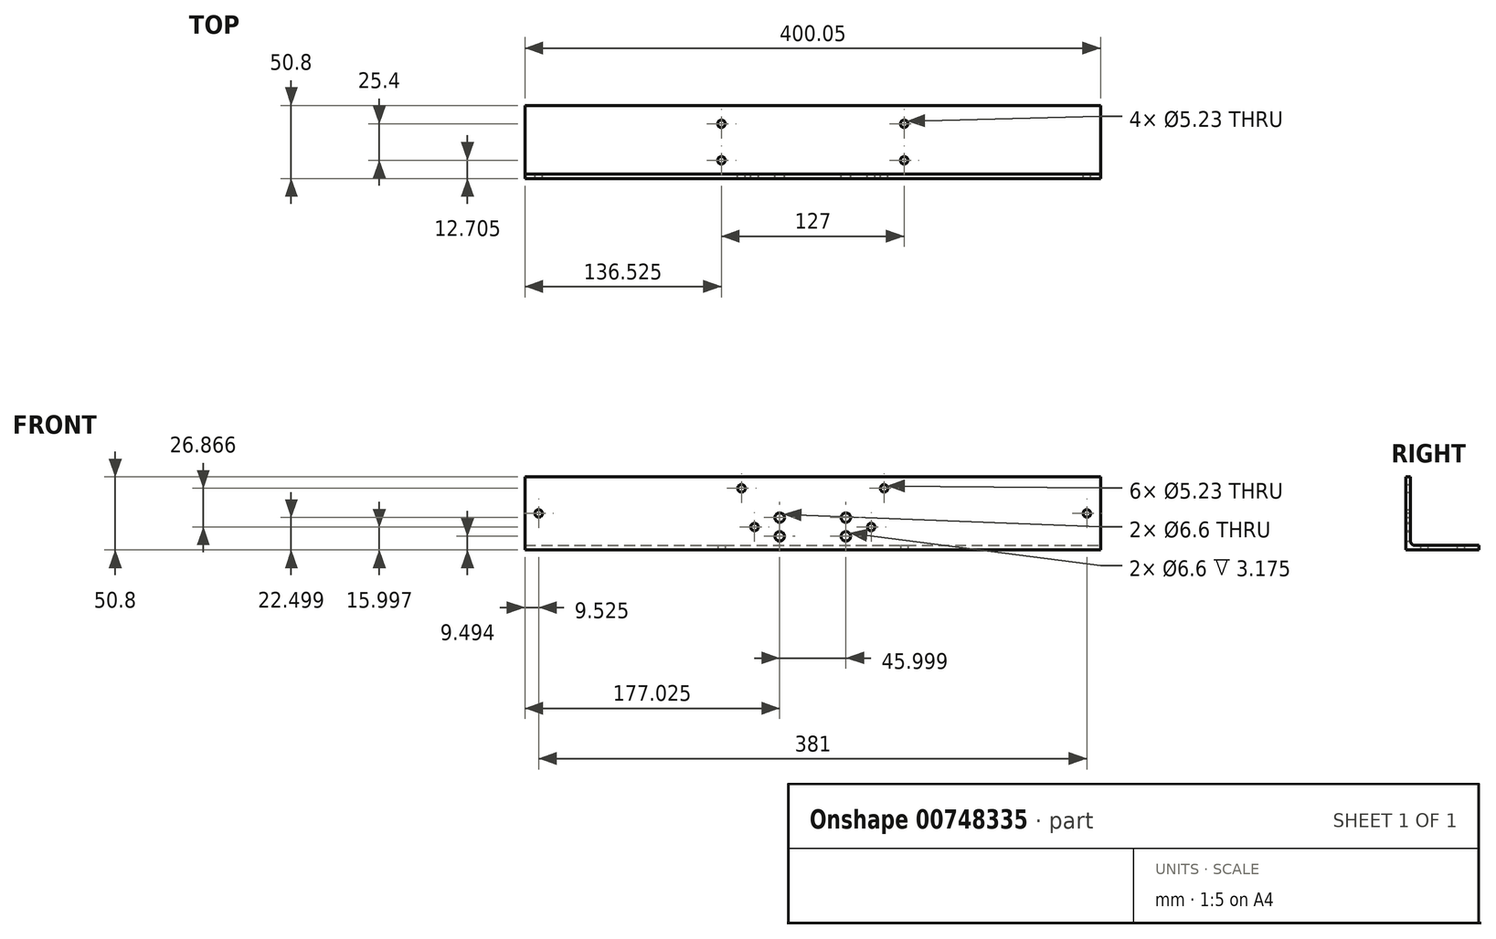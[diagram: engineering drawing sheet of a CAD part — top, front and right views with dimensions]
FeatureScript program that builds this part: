
annotation { "Feature Type Name" : "Feature", "Feature Type Description" : "" }
export const myFeature = defineFeature(function(context is Context, id is Id, definition is map)
    precondition{}
    {
        {
            var Q0;
            Q0=qCreatedBy(makeId("Right.planeOp"),FACE);
            var sketch = newSketch(context, id + "F0", { "sketchPlane" : qUnion([Q0])});
            skLineSegment(sketch, "E0", {"start": v(0, 0) * mm, "end": v(0, -44.45) * mm});
            skLineSegment(sketch, "E1", {"start": v(3.18, -47.63) * mm, "end": v(47.63, -47.62) * mm});
            skLineSegment(sketch, "E2.0", {"start": v(-3.17, -50.8) * mm, "end": v(47.63, -50.8) * mm});
            skLineSegment(sketch, "E2.1", {"start": v(-3.18, 0) * mm, "end": v(-3.17, -50.8) * mm});
            skLineSegment(sketch, "E3", {"start": v(-3.18, 0) * mm, "end": v(0, 0) * mm});
            skLineSegment(sketch, "E4", {"start": v(47.63, -47.62) * mm, "end": v(47.63, -50.8) * mm});
            skPoint(sketch, "E5.visualSharp", {"position": v(0, -47.63) * mm});
            skArc(sketch, "E5.filletArc", {"start": v(0, -44.45) * mm, "mid": v(0.93, -46.7) * mm, "end": v(3.18, -47.63) * mm});
            skSolve(sketch);
        }
        {
            var Q0;
            Q0=makeQuery(id+"F0.imprint","IMPRINT",FACE,{"disambiguationData":[TD([[makeQuery(id+"F0.imprint","IMPRINT",EDGE,{"derivedFrom":sQuery(id+"F0.wireOp",EDGE,"E0")}),-1.0]])]});
            extrude(context, id + "F1", {"entities" : qUnion([Q0]), "oppositeDirection" : true, "depth" : 400.05 * mm, "offsetDistance" : 25.4 * mm});
        }
        {
            var Q0;
            Q0=makeQuery(id+"F1.opExtrude","SWEPT_FACE",FACE,{"disambiguationData":[OSD([sQuery(id+"F0.wireOp",EDGE,"E0")])]});
            var sketch = newSketch(context, id + "F2", { "sketchPlane" : qUnion([Q0])});
            skLineSegment(sketch, "E6.right", {"start": v(9.53, 0) * mm, "end": v(9.53, -50.8) * mm, "construction": true});
            skLineSegment(sketch, "E7.right", {"start": v(390.53, 0) * mm, "end": v(390.53, -25.4) * mm, "construction": true});
            skLineSegment(sketch, "E8.left", {"start": v(9.53, 0) * mm, "end": v(9.53, -25.4) * mm, "construction": true});
            skLineSegment(sketch, "E9.right", {"start": v(390.53, -25.4) * mm, "end": v(390.53, -25.4) * mm});
            skCircle(sketch, "E10", {"center": v(9.53, -25.4) * mm, "radius": 2.62 * mm});
            skCircle(sketch, "E11", {"center": v(390.53, -25.4) * mm, "radius": 2.62 * mm});
            skLineSegment(sketch, "E12", {"start": v(9.53, -25.4) * mm, "end": v(390.53, -25.4) * mm, "construction": true});
            skLineSegment(sketch, "E13", {"start": v(200.03, 0) * mm, "end": v(200.03, -44.45) * mm, "construction": true});
            skLineSegment(sketch, "E14.0", {"start": v(240.51, 0) * mm, "end": v(240.51, -44.45) * mm, "construction": true});
            skLineSegment(sketch, "E15.0", {"start": v(159.54, 0) * mm, "end": v(159.54, -44.45) * mm, "construction": true});
            skPoint(sketch, "E16.middle", {"position": v(200.03, -25.4) * mm});
            skLineSegment(sketch, "E17", {"start": v(400.05, -34.8) * mm, "end": v(0, -34.8) * mm, "construction": true});
            skLineSegment(sketch, "E18.bottom", {"start": v(223.02, -28.3) * mm, "end": v(177.03, -28.3) * mm, "construction": true});
            skLineSegment(sketch, "E18.top", {"start": v(223.02, -41.3) * mm, "end": v(177.03, -41.3) * mm, "construction": true});
            skLineSegment(sketch, "E18.left", {"start": v(223.02, -28.3) * mm, "end": v(223.02, -41.3) * mm, "construction": true});
            skLineSegment(sketch, "E18.right", {"start": v(177.03, -28.3) * mm, "end": v(177.03, -41.3) * mm, "construction": true});
            skPoint(sketch, "E18.middle", {"position": v(200.03, -34.8) * mm});
            skCircle(sketch, "E19", {"center": v(177.03, -41.3) * mm, "radius": 3.3 * mm});
            skCircle(sketch, "E20", {"center": v(223.02, -41.3) * mm, "radius": 3.3 * mm});
            skCircle(sketch, "E21", {"center": v(177.03, -28.3) * mm, "radius": 3.3 * mm});
            skCircle(sketch, "E22", {"center": v(223.02, -28.3) * mm, "radius": 3.3 * mm});
            skCircle(sketch, "E23", {"center": v(159.44, -34.8) * mm, "radius": 2.62 * mm});
            skCircle(sketch, "E24", {"center": v(240.51, -34.8) * mm, "radius": 2.62 * mm});
            skLineSegment(sketch, "E25", {"start": v(0, -7.94) * mm, "end": v(400.05, -7.94) * mm, "construction": true});
            skCircle(sketch, "E26", {"center": v(249.58, -7.94) * mm, "radius": 2.62 * mm});
            skCircle(sketch, "E27", {"center": v(150.47, -7.94) * mm, "radius": 2.62 * mm});
            skSolve(sketch);
        }
        {
            var Q0;
            Q0 = qSketchRegion(id + "F2", true);
            extrude(context, id + "F3", {"entities" : qUnion([Q0]), "operationType" : NewBodyOperationType.REMOVE, "endBound" : BoundingType.THROUGH_ALL, "oppositeDirection" : true, "depth" : 25.4 * mm, "offsetDistance" : 25.4 * mm});
        }
        {
            var Q0;
            Q0=makeQuery(id+"F1.opExtrude","SWEPT_FACE",FACE,{"disambiguationData":[OSD([sQuery(id+"F0.wireOp",EDGE,"E2.0")])]});
            var sketch = newSketch(context, id + "F4", { "sketchPlane" : qUnion([Q0])});
            skLineSegment(sketch, "E28", {"start": v(-400.05, -22.23) * mm, "end": v(0, -22.23) * mm, "construction": true});
            skLineSegment(sketch, "E29", {"start": v(-200.03, 3.18) * mm, "end": v(-200.03, -47.63) * mm, "construction": true});
            skLineSegment(sketch, "E30", {"start": v(-263.53, 3.18) * mm, "end": v(-263.53, -47.63) * mm, "construction": true});
            skLineSegment(sketch, "E31", {"start": v(-136.53, 3.18) * mm, "end": v(-136.53, -47.63) * mm, "construction": true});
            skLineSegment(sketch, "E32", {"start": v(-400.05, -9.53) * mm, "end": v(0, -9.53) * mm, "construction": true});
            skLineSegment(sketch, "E33", {"start": v(-400.05, -34.93) * mm, "end": v(0, -34.93) * mm, "construction": true});
            skCircle(sketch, "E34", {"center": v(-136.53, -9.53) * mm, "radius": 2.62 * mm});
            skCircle(sketch, "E35", {"center": v(-136.53, -34.93) * mm, "radius": 2.62 * mm});
            skCircle(sketch, "E36", {"center": v(-263.53, -9.53) * mm, "radius": 2.62 * mm});
            skCircle(sketch, "E37", {"center": v(-263.53, -34.93) * mm, "radius": 2.62 * mm});
            skSolve(sketch);
        }
        {
            var Q0;
            Q0 = qSketchRegion(id + "F4", true);
            extrude(context, id + "F5", {"entities" : qUnion([Q0]), "operationType" : NewBodyOperationType.REMOVE, "endBound" : BoundingType.THROUGH_ALL, "oppositeDirection" : true, "depth" : 25.4 * mm, "offsetDistance" : 25.4 * mm});
        }
    });
